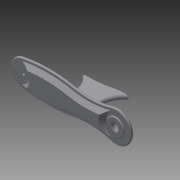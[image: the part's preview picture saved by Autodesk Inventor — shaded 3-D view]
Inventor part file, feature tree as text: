
AUTODESK INVENTOR PART (.ipt)
format: ipt  version: 2015 (Build 190159000, 159)  size: 638,464 bytes
history: native  units: mm
features: extrude x16, sketch x15, fillet x5, chamfer x2
ambient origin geometry x8: Origin, YZ Plane, XZ Plane, XY Plane, X Axis, Y Axis, Z Axis, Center Point
bodies: Solid1 (feature_tree)
feature tree (38):
  extrude  "Extrusion1"  Depth=50.0mm
  extrude  "Extrusion2"  Depth=15.0mm
  extrude  "Extrusion3"  Depth=5.0mm TaperAngle=0.0deg
  extrude  "Extrusion4"  Depth=18.1mm
  extrude  "Extrusion5"  Depth=20.0mm
  extrude  "Extrusion6"  Depth=9.5mm
  sketch  "Sketch7"  dims[d15=9.9mm d16=9.5mm]
  extrude  "Extrusion7"  Depth=9.5mm
  chamfer  "Chamfer1"  Distance=5.0mm
  extrude  "Extrusion8"  Depth=2.0mm
  extrude  "Extrusion17"  Depth=5.0mm TaperAngle=0.0deg
  chamfer  "Chamfer2"  Distance=5.0mm
  extrude  "Extrusion25"  Depth=5.0mm TaperAngle=0.0deg
  extrude  "Extrusion26"  Depth=20.0mm
  extrude  "Extrusion27"  Depth=30.0mm
  sketch  "Sketch30"  dims[d26=2.0mm d29=2.0mm]
  extrude  "Extrusion28"  Depth=7.3mm TaperAngle=0.0deg
  extrude  "Extrusion32"  Depth=7.3mm TaperAngle=45.0deg
  extrude  "Extrusion33"  Depth=12.3mm TaperAngle=0.0deg
  extrude  "Extrusion34"  Depth=6.0mm
  fillet  "Fillet5"  Radius=5.0mm
  fillet  "Fillet6"  Radius=7.3mm
  fillet  "Fillet7"  Radius=35.0mm
  fillet  "Fillet8"  Radius=2.0mm
  fillet  "Fillet9"  Radius=10.0mm
  sketch  "Sketch1"  dims[d0=180.0mm d1=50.0mm]
  sketch  "Sketch2"  dims[d2=5.0mm d3=0.0mm d4=15.0mm]
  sketch  "Sketch3"  dims[d5=15.0mm d6=5.0mm d7=0.0mm]
  sketch  "Sketch4"  dims[d9=34.65mm d10=18.1mm]
  sketch  "Sketch5"  dims[d11=55.0mm d12=20.0mm]
  sketch  "Sketch6"  dims[d13=40.2mm d14=9.5mm]
  sketch  "Sketch8"  dims[d17=9.9mm]
  sketch  "Sketch9"  dims[d18=3.0mm]
  sketch  "Sketch18"  dims[d19=3.0mm]
  sketch  "Sketch27"  dims[d20=3.0mm]
  sketch  "Sketch28"  dims[d21=3.0mm]
  sketch  "Sketch29"  dims[d22=13.6mm d23=5.0mm d24=0.0mm]
  sketch  "Sketch33"  dims[d30=2.0mm d31=5.0mm d32=0.0mm d63=5.0mm d64=0.0mm d65=5.0mm d66=0.0mm d72=20.0mm d73=30.0mm d74=7.3mm d75=0.0mm d76=7.3mm d77=2.0mm d78=45.0deg d79=12.3mm d80=0.0mm d114=6.0mm d115=5.0mm d116=0.0mm d117=7.3mm d118=2.0mm d119=45.0deg d155=35.0mm d156=2.0mm d157=0.0mm d158=10.0mm d159=2.0mm d160=0.0mm d161=5.0mm d162=0.0mm d177=72.6mm d178=0.0mm d183=20.0mm d184=80.0mm d192=80.0mm d195=10.0mm d196=20.0mm d197=10.0mm d199=72.6mm d200=0.0mm d201=45.0mm d202=45.0mm d203=20.0mm d204=0.0mm d205=72.6mm d206=0.0mm d211=2.0mm d212=5.0mm d213=2.0mm d214=1.0mm d215=5.0mm]
